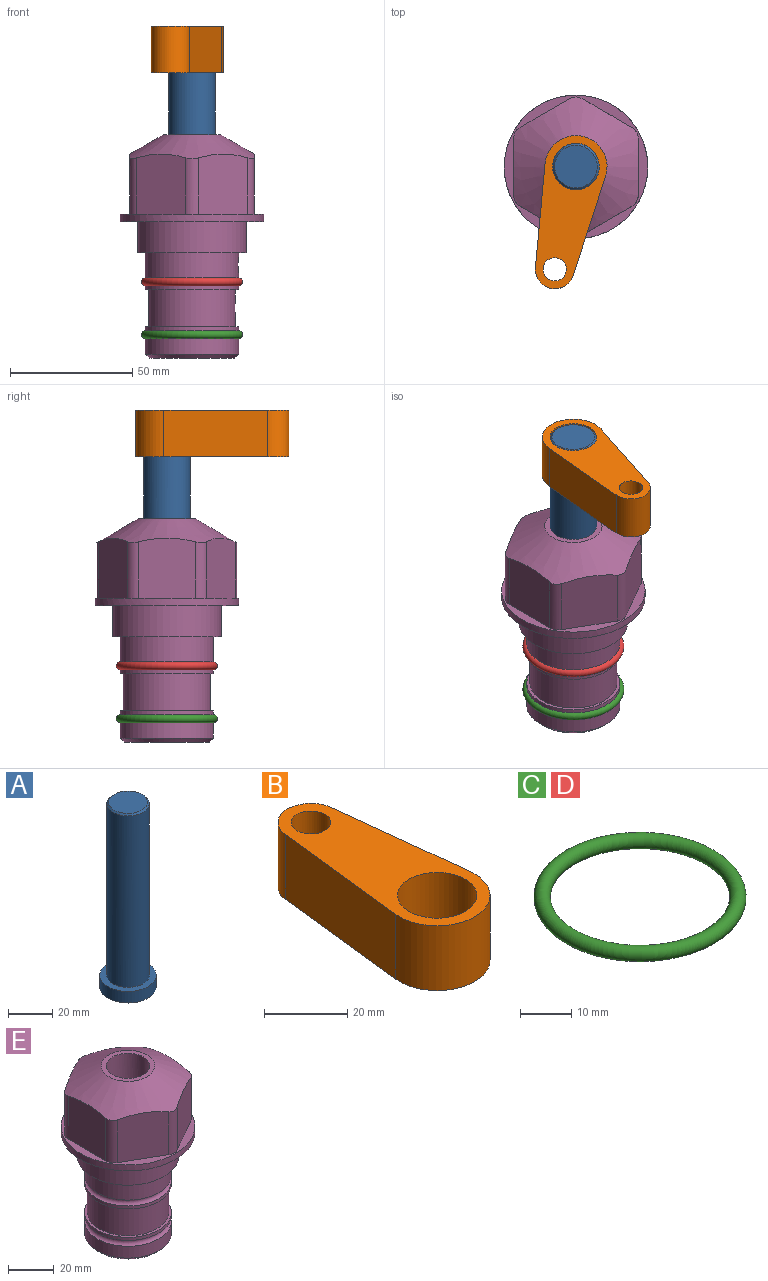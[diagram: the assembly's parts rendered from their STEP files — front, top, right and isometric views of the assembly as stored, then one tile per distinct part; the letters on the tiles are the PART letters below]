
ASSEMBLY  parts=5 mates=3
PART A: 6 faces, bbox 25.4x25.4x101.6 mm
  f0: plane 17.46x17.46mm, normal (0,0,1), area 239.5mm2, adj f5
  f1: plane 25.4x25.4mm, normal (0,0,-1), area 506.7mm2, adj f2
  f2: cylinder r=12.7mm len=25.4mm, axis (0,0,1), area 506.7mm2, adj f1,f3
  f3: plane 25.4x25.4mm, normal (0,0,1), area 221.7mm2, adj f2,f4
  f4: cylinder r=9.53mm len=94.46mm, axis (0,0,1), area 5653mm2, adj f3,f5
  f5: cone r=8.73mm half-angle=45deg, axis (0,0,-1), area 64.4mm2, adj f0,f4
PART B: 8 faces, bbox 25.4x63.5x19.1 mm
  f0: cylinder r=12.7mm len=25.4mm, axis (0,0,-1), area 813.9mm2, adj f1,f3,f6,f7
  f1: plane 42.33x19.05mm, normal (0.99,0.11,0), area 811.5mm2, adj f0,f2,f6,f7
  f2: cylinder r=7.94mm len=19.05mm, axis (0,0,-1), area 441.4mm2, adj f1,f3,f6,f7
  f3: plane 42.33x19.05mm, normal (-0.99,0.11,0), area 811.5mm2, adj f0,f2,f6,f7
  f4: cylinder r=9.53mm len=19.05mm, axis (0,0,-1), area 1140.1mm2, adj f6,f7
  f5: cylinder r=4.76mm len=19.05mm, axis (0,0,-1), area 570mm2, adj f6,f7
  f6: plane 63.5x25.4mm, normal (0,0,1), area 886.1mm2, adj f0,f1,f2,f3,f4,f5
  f7: plane 63.5x25.4mm, normal (0,0,-1), area 886.1mm2, adj f0,f1,f2,f3,f4,f5
PART C: 1 faces, bbox 44.7x44.7x3.2 mm
  f0: torus R=19.05mm, axis (0,0,1), area 1193.9mm2
PART D: same geometry as C
PART E: 36 faces, bbox 58.7x58.7x91.2 mm
  f0: cylinder r=17.78mm len=35.56mm, axis (0,0,1), area 1670.8mm2, adj f23,f24,f31
  f1: cylinder r=19.05mm len=38.1mm, axis (0,0,1), area 1191.9mm2, adj f26,f27,f30
  f2: plane 58.66x58.66mm, normal (0,0,-1), area 1150.6mm2, adj f3,f28
  f3: cylinder r=29.33mm len=58.66mm, axis (0,0,-1), area 585.1mm2, adj f2,f4
  f4: plane 58.66x58.66mm, normal (0,0,1), area 475.9mm2, adj f3,f5,f6,f7,f8,f9,f10,f11
  f5: plane 24.5x20.32mm, normal (-0.5,0.87,0), area 562.8mm2, adj f4,f15,f16,f17
  f6: plane 24.5x20.32mm, normal (0.5,0.87,0), area 562.8mm2, adj f4,f14,f15,f17
  f7: plane 24.5x23.48mm, normal (1,0,0), area 562.8mm2, adj f4,f13,f14,f17
  f8: plane 24.5x20.32mm, normal (0.5,-0.87,0), area 562.8mm2, adj f4,f12,f13,f17
  f9: plane 24.5x20.32mm, normal (-0.5,-0.87,0), area 562.8mm2, adj f4,f11,f12,f17
  f10: plane 24.5x23.48mm, normal (-1,0,0), area 562.8mm2, adj f4,f11,f16,f17
  f11: cylinder r=5.08mm len=23.01mm, axis (0,0,-1), area 121.2mm2, adj f4,f9,f10,f17
  f12: cylinder r=5.08mm len=23.01mm, axis (0,0,-1), area 121.2mm2, adj f4,f8,f9,f17
  f13: cylinder r=5.08mm len=23.01mm, axis (0,0,-1), area 121.2mm2, adj f4,f7,f8,f17
  f14: cylinder r=5.08mm len=23.01mm, axis (0,0,-1), area 121.2mm2, adj f4,f6,f7,f17
  f15: cylinder r=5.08mm len=23.01mm, axis (0,0,-1), area 121.2mm2, adj f4,f5,f6,f17
  f16: cylinder r=5.08mm len=23.01mm, axis (0,0,-1), area 121.2mm2, adj f4,f5,f10,f17
  f17: cone r=11.73mm half-angle=60deg, axis (0,0,-1), area 2071.8mm2, adj f5,f6,f7,f8,f9,f10,f11,f12
  f18: plane 23.46x23.46mm, normal (0,0,1), area 147.4mm2, adj f17,f35
  f19: plane 34.93x34.93mm, normal (0,0,-1), area 958mm2, adj f29
  f20: cylinder r=19.05mm len=38.1mm, axis (0,0,1), area 760.1mm2, adj f21,f29
  f21: torus R=19.05mm, axis (0,0,1), area 565.3mm2, adj f20,f22
  f22: cylinder r=19.05mm len=38.1mm, axis (0,0,1), area 190mm2, adj f21,f23
  f23: plane 38.1x38.1mm, normal (0,0,1), area 146.9mm2, adj f0,f22
  f24: plane 38.1x38.1mm, normal (0,0,-1), area 146.9mm2, adj f0,f25
  f25: cylinder r=19.05mm len=38.1mm, axis (0,0,1), area 190mm2, adj f24,f26
  f26: torus R=19.05mm, axis (0,0,1), area 565.3mm2, adj f1,f25
  f27: plane 44.45x44.45mm, normal (0,0,-1), area 411.7mm2, adj f1,f28
  f28: cylinder r=22.23mm len=44.45mm, axis (0,0,1), area 1773.5mm2, adj f2,f27
  f29: cone r=19.05mm half-angle=45deg, axis (0,0,1), area 257.5mm2, adj f19,f20
  f30: cylinder r=3.17mm len=6.75mm, axis (-1,0,0), area 128mm2, adj f1,f33
  f31: cylinder r=3.17mm len=6.35mm, axis (-1,0,0), area 102.5mm2, adj f0,f33
  f32: plane 25.4x25.4mm, normal (0,0,1), area 506.7mm2, adj f33
  f33: cylinder r=12.7mm len=66.42mm, axis (0,0,-1), area 5236.2mm2, adj f30,f31,f32,f34
  f34: cone r=9.53mm half-angle=30deg, axis (0,0,-1), area 443.4mm2, adj f33,f35
  f35: cylinder r=9.53mm len=19.05mm, axis (0,0,-1), area 849mm2, adj f18,f34
PLACE A rot(axis=(0,0,-1),101.7deg) t=(0,0,6.38)mm
PLACE B rot(axis=(0,0,1),168.3deg) t=(0,0,60.99)mm
PLACE C t=(0,0,-21.59)mm
PLACE D at identity
PLACE E at identity fixed
MATE fastened C.f0 <-> E.f0  axis (0,0,1) through (0,0,-46.1)mm
MATE cylindrical A.f2 <-> E.f0  axis (0,0,1) through (0,0,32.01)mm
MATE fastened B.f0 <-> A.f2  axis (0,0,1) through (0,0,80.04)mm
